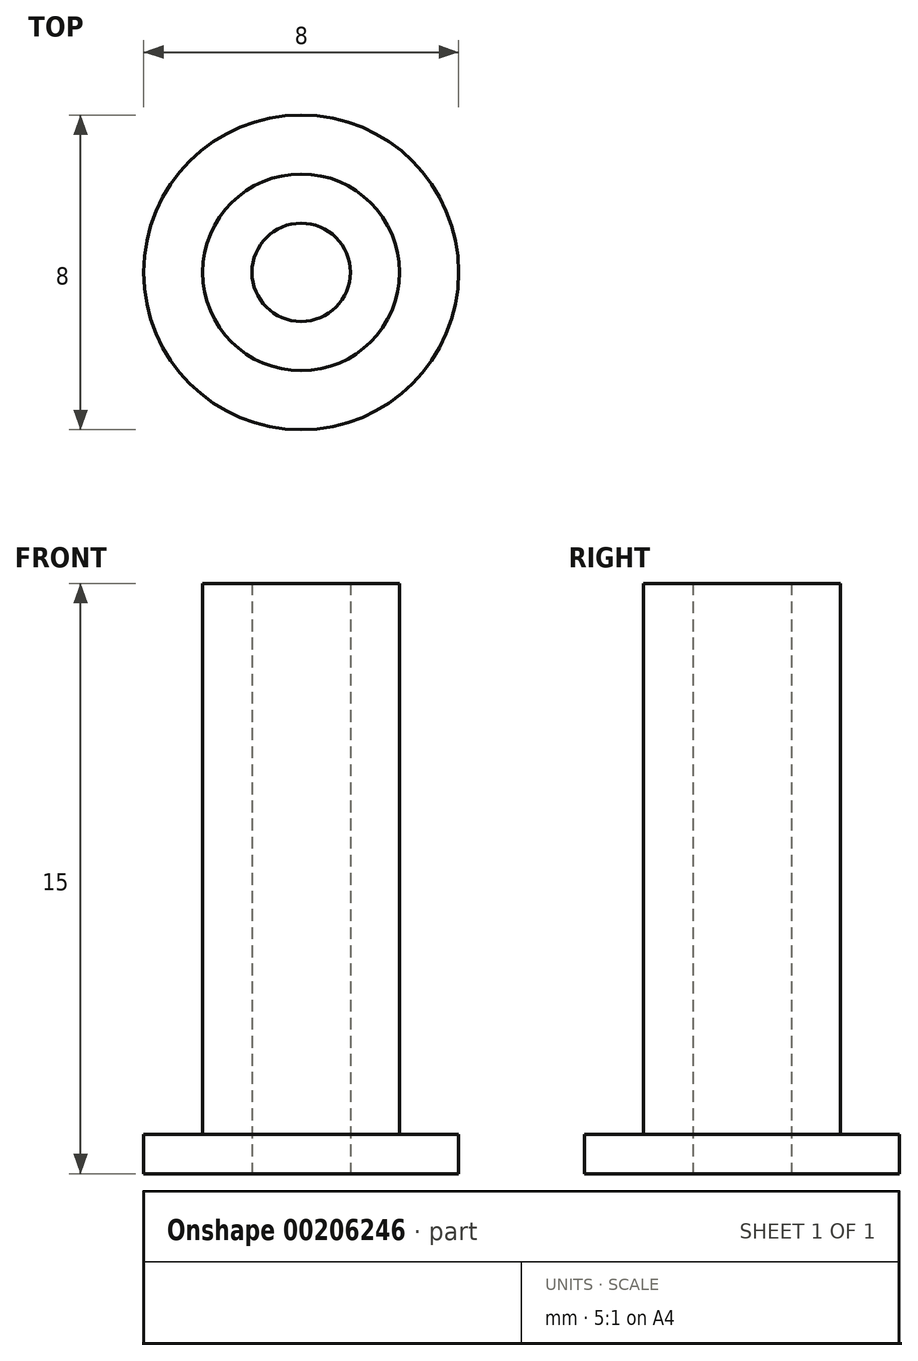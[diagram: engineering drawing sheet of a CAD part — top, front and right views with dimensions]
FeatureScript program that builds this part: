
annotation { "Feature Type Name" : "Feature", "Feature Type Description" : "" }
export const myFeature = defineFeature(function(context is Context, id is Id, definition is map)
    precondition{}
    {
        {
            var Q0;
            Q0=qCreatedBy(makeId("Top.planeOp"),FACE);
            var sketch = newSketch(context, id + "F0", { "sketchPlane" : qUnion([Q0])});
            skCircle(sketch, "E0", {"center": v(0, 0) * mm, "radius": 2.5 * mm});
            skCircle(sketch, "E1", {"center": v(0, 0) * mm, "radius": 1.25 * mm});
            skSolve(sketch);
        }
        {
            var Q0;
            Q0=makeQuery(id+"F0.imprint","IMPRINT",FACE,{"disambiguationData":[TD([[makeQuery(id+"F0.imprint","IMPRINT",EDGE,{"derivedFrom":sQuery(id+"F0.wireOp",EDGE,"E0")}),1.0]])]});
            extrude(context, id + "F1", {"entities" : qUnion([Q0]), "depth" : 15 * mm});
        }
        {
            var Q0;
            Q0=makeQuery(id+"F1.opExtrude","CAP_FACE",FACE,{"disambiguationData":[OSD([sQuery(id+"F0.wireOp",EDGE,"E0"),sQuery(id+"F0.wireOp",EDGE,"E1")])],"isStart":true});
            var sketch = newSketch(context, id + "F2", { "sketchPlane" : qUnion([Q0])});
            skCircle(sketch, "E2", {"center": v(0, 0) * mm, "radius": 4 * mm});
            skSolve(sketch);
        }
        {
            var Q0;
            Q0=makeQuery(id+"F2.imprint","IMPRINT",FACE,{"disambiguationData":[TD([[makeQuery(id+"F2.imprint","IMPRINT",EDGE,{"derivedFrom":sQuery(id+"F2.wireOp",EDGE,"E2")}),1.0]])]});
            extrude(context, id + "F3", {"entities" : qUnion([Q0]), "operationType" : NewBodyOperationType.ADD, "oppositeDirection" : true, "depth" : 1 * mm});
        }
    });
